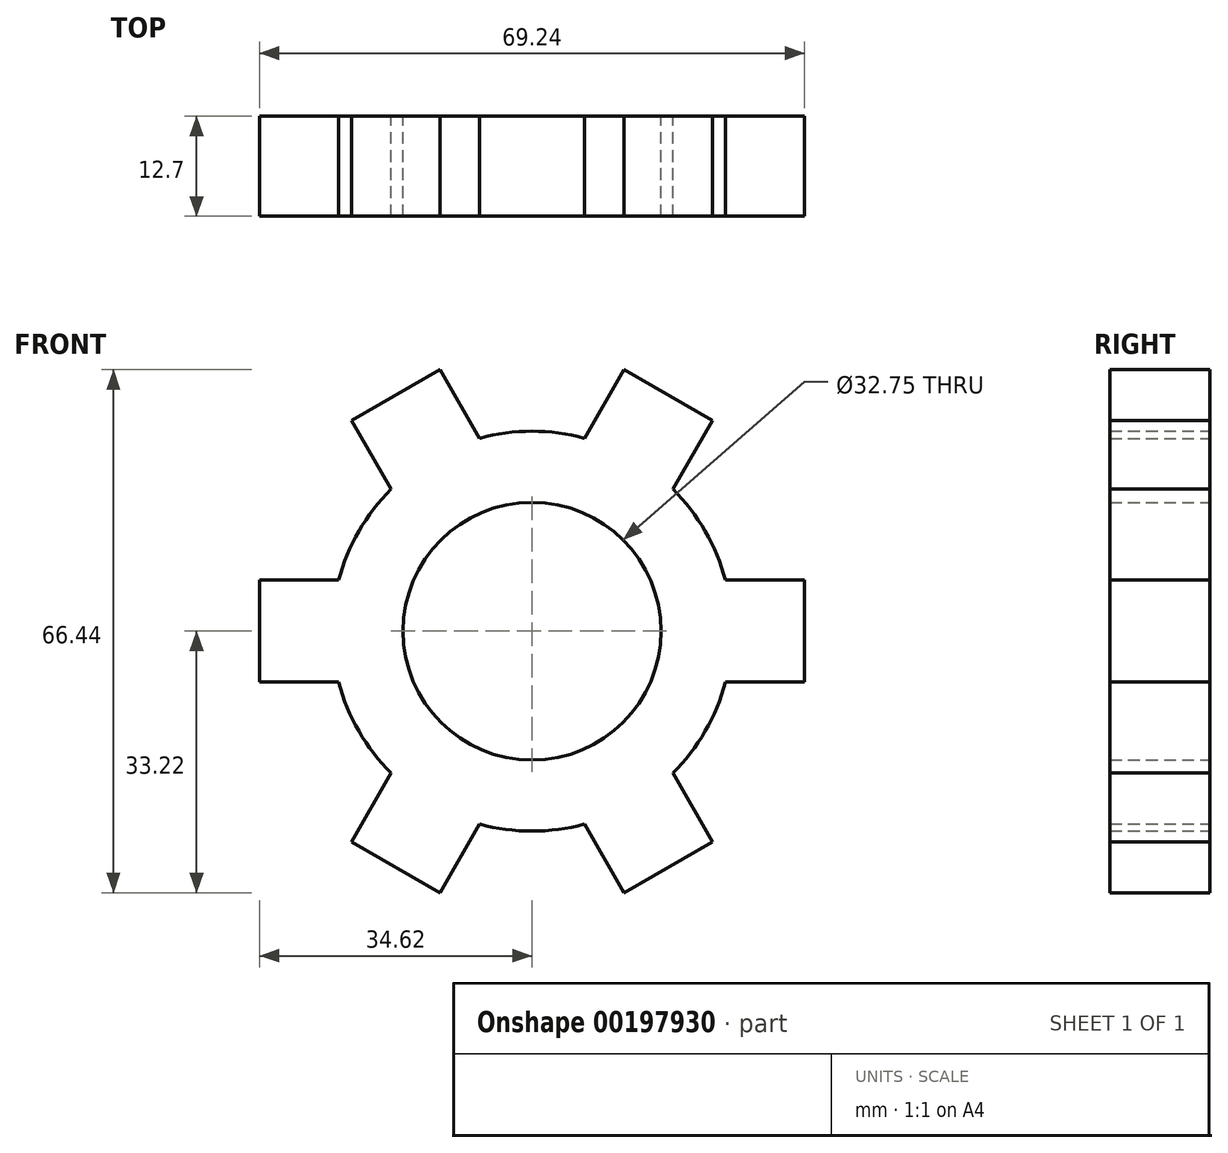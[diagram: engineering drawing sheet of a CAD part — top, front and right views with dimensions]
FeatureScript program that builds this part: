
annotation { "Feature Type Name" : "Feature", "Feature Type Description" : "" }
export const myFeature = defineFeature(function(context is Context, id is Id, definition is map)
    precondition{}
    {
        {
            var Q0;
            Q0=qCreatedBy(makeId("Front.planeOp"),FACE);
            var sketch = newSketch(context, id + "F0", { "sketchPlane" : qUnion([Q0])});
            skCircle(sketch, "E0", {"center": v(0, 0) * mm, "radius": 25.4 * mm});
            skSolve(sketch);
        }
        {
            var Q0;
            Q0 = qSketchRegion(id + "F0", true);
            extrude(context, id + "F1", {"entities" : qUnion([Q0]), "endBound" : BoundingType.SYMMETRIC, "depth" : 12.7 * mm});
        }
        {
            var Q0;
            Q0=makeQuery(id+"F1.opExtrude","CAP_FACE",FACE,{"disambiguationData":[OSD([sQuery(id+"F0.wireOp",EDGE,"E0")])],"isStart":false});
            var sketch = newSketch(context, id + "F2", { "sketchPlane" : qUnion([Q0])});
            skLineSegment(sketch, "E1", {"start": v(0, 0) * mm, "end": v(-24.53, 6.57) * mm});
            skLineSegment(sketch, "E2", {"start": v(0, 0) * mm, "end": v(-24.53, -6.57) * mm});
            skLineSegment(sketch, "E3", {"start": v(0, 0) * mm, "end": v(-25.4, 0) * mm});
            skLineSegment(sketch, "E4", {"start": v(-24.53, -6.57) * mm, "end": v(-24.53, 6.57) * mm});
            skLineSegment(sketch, "E5.0", {"start": v(-24.46, -6.48) * mm, "end": v(-24.46, 6.48) * mm});
            skLineSegment(sketch, "E5.1", {"start": v(-0.29, 0) * mm, "end": v(-24.46, -6.48) * mm});
            skLineSegment(sketch, "E5.2", {"start": v(-0.29, 0) * mm, "end": v(-24.46, 6.48) * mm});
            skLineSegment(sketch, "E6.0", {"start": v(-34.62, -6.48) * mm, "end": v(-34.62, 6.48) * mm});
            skLineSegment(sketch, "E7", {"start": v(-24.46, -6.48) * mm, "end": v(-34.62, -6.48) * mm});
            skLineSegment(sketch, "E8", {"start": v(-24.46, 6.48) * mm, "end": v(-34.62, 6.48) * mm});
            skSolve(sketch);
        }
        {
            var Q0;
            Q0 = qSketchRegion(id + "F2", true);
            extrude(context, id + "F3", {"entities" : qUnion([Q0]), "operationType" : NewBodyOperationType.ADD, "oppositeDirection" : true, "depth" : 12.7 * mm});
        }
        {
            var Q0;
            Q0=qCreatedBy(makeId("Right.planeOp"),FACE);
            var sketch = newSketch(context, id + "F4", { "sketchPlane" : qUnion([Q0])});
            skLineSegment(sketch, "E9", {"start": v(0, 0) * mm, "end": v(-47.77, 0) * mm});
            skSolve(sketch);
        }
        {
            var Q0;
            Q0=makeQuery(id+"F1.opExtrude","SWEPT_BODY",BODY,{"disambiguationData":[OSD([sQuery(id+"F0.wireOp",EDGE,"E0")])]});
            var Q1;
            Q1=sQuery(id+"F4.wireOp",EDGE,"E9");
            circularPattern(context, id + "F5", {"operationType" : NewBodyOperationType.ADD, "entities" : qUnion([Q0]), "axis" : qUnion([Q1]), "angle" : 360 * degree, "instanceCount" : 6, "equalSpace" : true});
        }
        {
            var Q0;
            {var subQ0=makeQuery(id+"F3.boolean.opBoolean","MERGE",FACE,{"derivedFrom":[makeQuery(id+"F1.opExtrude","CAP_FACE",FACE,{"disambiguationData":[OSD([sQuery(id+"F0.wireOp",EDGE,"E0")])],"isStart":false}),makeQuery(id+"F3.opExtrude","CAP_FACE",FACE,{"disambiguationData":[OSD([sQuery(id+"F2.wireOp",EDGE,"E1"),sQuery(id+"F2.wireOp",EDGE,"E2"),sQuery(id+"F2.wireOp",EDGE,"E4"),sQuery(id+"F2.wireOp",EDGE,"E5.0"),sQuery(id+"F2.wireOp",EDGE,"E5.1"),sQuery(id+"F2.wireOp",EDGE,"E5.2"),sQuery(id+"F2.wireOp",EDGE,"E6.0"),sQuery(id+"F2.wireOp",EDGE,"E7"),sQuery(id+"F2.wireOp",EDGE,"E8")])],"isStart":true})]});Q0=makeQuery(id+"F5.boolean.opBoolean","MERGE",FACE,{"derivedFrom":[subQ0,makeQuery(id+"F5.opPattern","COPY",FACE,{"derivedFrom":subQ0,"instanceName":"1"}),makeQuery(id+"F5.opPattern","COPY",FACE,{"derivedFrom":subQ0,"instanceName":"2"}),makeQuery(id+"F5.opPattern","COPY",FACE,{"derivedFrom":subQ0,"instanceName":"3"}),makeQuery(id+"F5.opPattern","COPY",FACE,{"derivedFrom":subQ0,"instanceName":"4"}),makeQuery(id+"F5.opPattern","COPY",FACE,{"derivedFrom":subQ0,"instanceName":"5"})]});}
            var sketch = newSketch(context, id + "F6", { "sketchPlane" : qUnion([Q0])});
            skCircle(sketch, "E10", {"center": v(0, 0) * mm, "radius": 6.48 * mm});
            skSolve(sketch);
        }
        {
            var Q0;
            Q0 = qSketchRegion(id + "F6", true);
            extrude(context, id + "F7", {"entities" : qUnion([Q0]), "operationType" : NewBodyOperationType.REMOVE, "depth" : 12.7 * mm});
        }
        {
            var Q0;
            {var subQ0=makeQuery(id+"F3.boolean.opBoolean","MERGE",FACE,{"derivedFrom":[makeQuery(id+"F1.opExtrude","CAP_FACE",FACE,{"disambiguationData":[OSD([sQuery(id+"F0.wireOp",EDGE,"E0")])],"isStart":true}),makeQuery(id+"F3.opExtrude","CAP_FACE",FACE,{"disambiguationData":[OSD([sQuery(id+"F2.wireOp",EDGE,"E1"),sQuery(id+"F2.wireOp",EDGE,"E2"),sQuery(id+"F2.wireOp",EDGE,"E4"),sQuery(id+"F2.wireOp",EDGE,"E5.0"),sQuery(id+"F2.wireOp",EDGE,"E5.1"),sQuery(id+"F2.wireOp",EDGE,"E5.2"),sQuery(id+"F2.wireOp",EDGE,"E6.0"),sQuery(id+"F2.wireOp",EDGE,"E7"),sQuery(id+"F2.wireOp",EDGE,"E8")])],"isStart":false})]});Q0=makeQuery(id+"F5.boolean.opBoolean","MERGE",FACE,{"derivedFrom":[subQ0,makeQuery(id+"F5.opPattern","COPY",FACE,{"derivedFrom":subQ0,"instanceName":"1"}),makeQuery(id+"F5.opPattern","COPY",FACE,{"derivedFrom":subQ0,"instanceName":"2"}),makeQuery(id+"F5.opPattern","COPY",FACE,{"derivedFrom":subQ0,"instanceName":"3"}),makeQuery(id+"F5.opPattern","COPY",FACE,{"derivedFrom":subQ0,"instanceName":"4"}),makeQuery(id+"F5.opPattern","COPY",FACE,{"derivedFrom":subQ0,"instanceName":"5"})]});}
            var sketch = newSketch(context, id + "F8", { "sketchPlane" : qUnion([Q0])});
            skCircle(sketch, "E11", {"center": v(0, 0) * mm, "radius": 16.38 * mm});
            skSolve(sketch);
        }
        {
            var Q0;
            Q0=makeQuery(id+"F8.imprint","IMPRINT",FACE,{"disambiguationData":[TD([[makeQuery(id+"F8.imprint","IMPRINT",EDGE,{"derivedFrom":sQuery(id+"F8.wireOp",EDGE,"E11")}),1.0]])]});
            extrude(context, id + "F9", {"entities" : qUnion([Q0]), "operationType" : NewBodyOperationType.REMOVE, "oppositeDirection" : true, "depth" : 12.7 * mm});
        }
    });
